# Revit family: Haworth_Cotone_CollaborativeTable_PRELIMINARY
name_source: partatom
category: Furniture
revit_build: Autodesk Revit 2018 (Build: 20170223_1515(x64)
units: mm (PartAtom-declared; Revit-internal decimal feet)

## family parameters
Always vertical = Yes
Cut with Voids When Loaded = No
OmniClass Number = 23.40.70.14.64.21
OmniClass Title = Systems Furniture
Room Calculation Point = No
Shared = No
Work Plane-Based = No

## types (5) — shared parameters
Actual Height = 29.1 "
Assembly Code = E2020200
Custom Size = No
Description = Haworth - Cassina - Cotone - Collaborative Table
Glide Finish = Haworth _ Polymer _ Black
Manufacturer = Haworth
Model = Haworth - Cassina - Cotone
Revision Number = 1
Size = Verify Final Dim. w/ Haworth
Sustainability Info = https://www.haworth.com
URL = https://www.haworth.com
URL - Product = https://www.haworth.com
Warranty = http://www.haworth.com

## per-type parameters (varying)
| type | Actual Depth | Actual Width | Depth | Double Frame | Extra Large | Extra Small | Large | Medium | Single Frame | Small | Width |
| 55.1w x 55.1d | 55.1 " | 55.1 " | 55.1 " | No | Yes | No | No | No | Yes | No | 55.1 " |
| 78.7w x 35.4d | 35.4 " | 78.7 " | 35.4 " | No | No | No | No | No | Yes | Yes | 78.7 " |
| 94.5w x 35.4d | 35.4 " | 94.5 " | 35.4 " | Yes | No | No | No | Yes | No | No | 94.5 " |
| 110.2w x 35.4d | 35.4 " | 110.2 " | 35.4 " | Yes | No | No | Yes | No | No | No | 110.2 " |
| 63w x 31.5d | 31.5 " | 63 " | 31.5 " | No | No | Yes | No | No | No | No | 63 " |

type visibility flags: 5 boolean params named "<type name>" — each type sets only its own to Yes (folded from table)

## geometry (parser evidence)
native form markers: Sweep x8
no freeform markers — native parametric forms only
